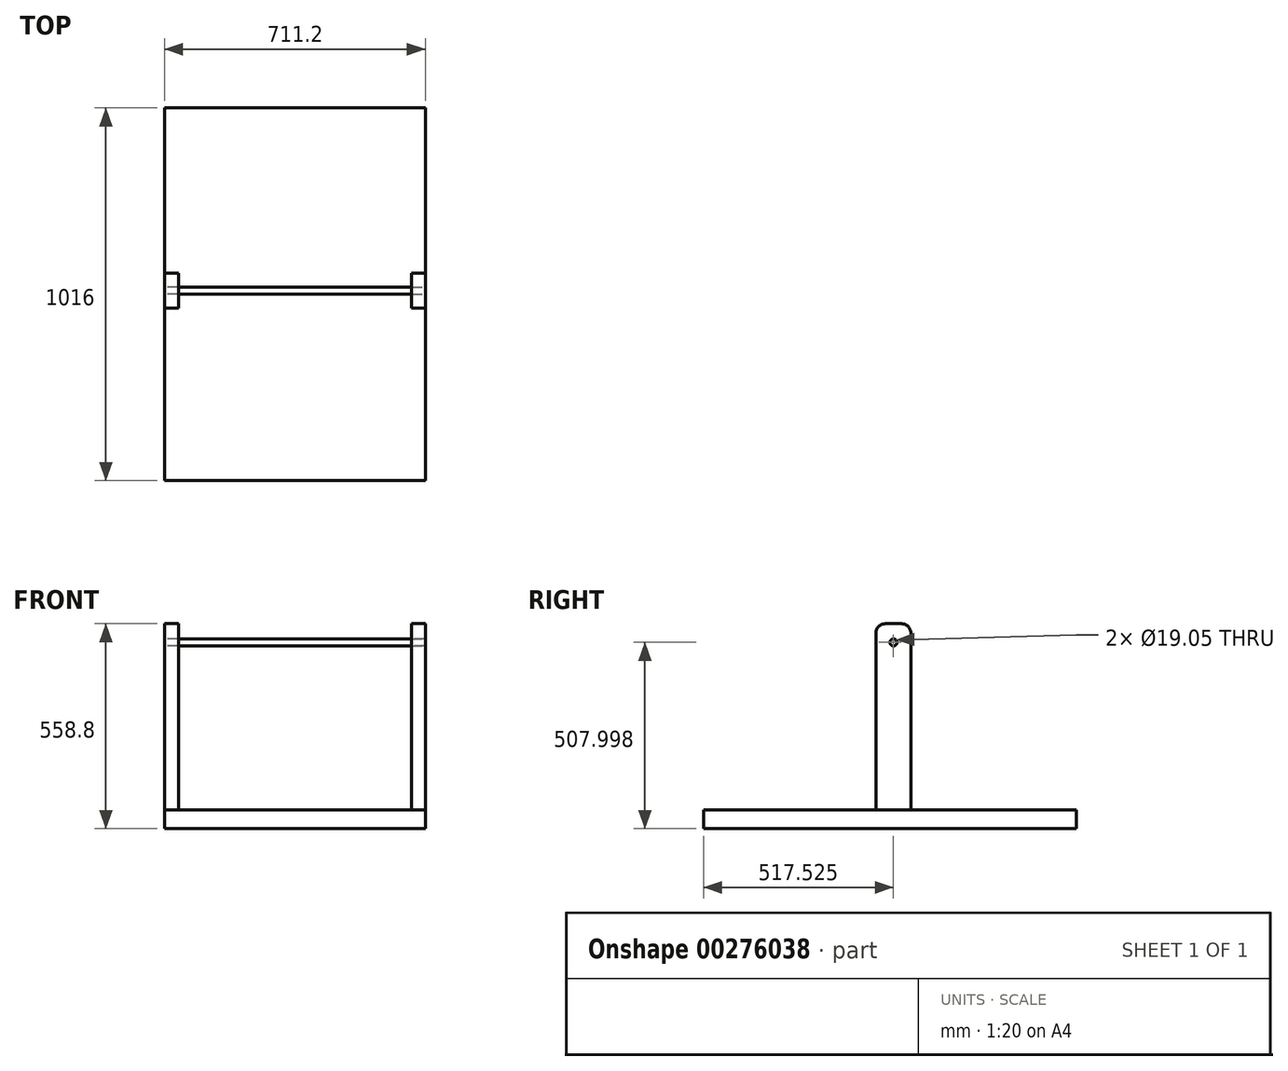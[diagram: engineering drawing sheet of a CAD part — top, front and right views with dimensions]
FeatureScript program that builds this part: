
annotation { "Feature Type Name" : "Feature", "Feature Type Description" : "" }
export const myFeature = defineFeature(function(context is Context, id is Id, definition is map)
    precondition{}
    {
        {
            var Q0;
            Q0=qCreatedBy(makeId("Front.planeOp"),FACE);
            var sketch = newSketch(context, id + "F0", { "sketchPlane" : qUnion([Q0])});
            skLineSegment(sketch, "E0", {"start": v(-62.9, 34.99) * mm, "end": v(-62.9, -15.81) * mm});
            skLineSegment(sketch, "E1", {"start": v(-62.9, -15.81) * mm, "end": v(648.3, -15.81) * mm});
            skLineSegment(sketch, "E2", {"start": v(648.3, -15.81) * mm, "end": v(648.3, 34.99) * mm});
            skLineSegment(sketch, "E3", {"start": v(648.3, 34.99) * mm, "end": v(-62.9, 34.99) * mm});
            skSolve(sketch);
        }
        {
            var Q0;
            Q0 = qSketchRegion(id + "F0", true);
            extrude(context, id + "F1", {"entities" : qUnion([Q0]), "depth" : 1016 * mm});
        }
        {
            var Q0;
            Q0=makeQuery(id+"F1.opExtrude","SWEPT_FACE",FACE,{"disambiguationData":[OSD([sQuery(id+"F0.wireOp",EDGE,"E0")])]});
            var sketch = newSketch(context, id + "F2", { "sketchPlane" : qUnion([Q0])});
            skLineSegment(sketch, "E4", {"start": v(450.85, 34.99) * mm, "end": v(450.85, 517.59) * mm});
            skLineSegment(sketch, "E5", {"start": v(546.1, 34.99) * mm, "end": v(546.1, 517.59) * mm});
            skLineSegment(sketch, "E6", {"start": v(546.1, 34.99) * mm, "end": v(450.85, 34.99) * mm});
            skLineSegment(sketch, "E7", {"start": v(476.25, 542.99) * mm, "end": v(520.7, 542.99) * mm});
            skLineSegment(sketch, "E8", {"start": v(498.48, 542.99) * mm, "end": v(498.48, 492.19) * mm});
            skCircle(sketch, "E9", {"center": v(498.48, 492.19) * mm, "radius": 9.53 * mm});
            skPoint(sketch, "E10.visualSharp", {"position": v(450.85, 542.99) * mm});
            skArc(sketch, "E10.filletArc", {"start": v(476.25, 542.99) * mm, "mid": v(458.29, 535.55) * mm, "end": v(450.85, 517.59) * mm});
            skPoint(sketch, "E11.visualSharp", {"position": v(546.1, 542.99) * mm});
            skArc(sketch, "E11.filletArc", {"start": v(546.1, 517.59) * mm, "mid": v(538.66, 535.55) * mm, "end": v(520.7, 542.99) * mm});
            skLineSegment(sketch, "E12", {"start": v(1016, 34.99) * mm, "end": v(0, 34.99) * mm});
            skSolve(sketch);
        }
        {
            var Q0;
            Q0 = qSketchRegion(id + "F2", true);
            extrude(context, id + "F3", {"entities" : qUnion([Q0]), "oppositeDirection" : true, "depth" : 38.1 * mm});
        }
        {
            var Q0;
            Q0=makeQuery(id+"F1.opExtrude","SWEPT_FACE",FACE,{"disambiguationData":[OSD([sQuery(id+"F0.wireOp",EDGE,"E2")])]});
            var sketch = newSketch(context, id + "F4", { "sketchPlane" : qUnion([Q0])});
            skLineSegment(sketch, "E13", {"start": v(-1016, 34.99) * mm, "end": v(-546.1, 34.99) * mm});
            skLineSegment(sketch, "E14", {"start": v(0, 34.99) * mm, "end": v(-450.85, 34.99) * mm});
            skLineSegment(sketch, "E15", {"start": v(-546.1, 34.99) * mm, "end": v(-546.1, 517.59) * mm});
            skLineSegment(sketch, "E16", {"start": v(-450.85, 34.99) * mm, "end": v(-450.85, 517.59) * mm});
            skLineSegment(sketch, "E17", {"start": v(-520.7, 542.99) * mm, "end": v(-476.25, 542.99) * mm});
            skPoint(sketch, "E18.visualSharp", {"position": v(-546.1, 542.99) * mm});
            skArc(sketch, "E18.filletArc", {"start": v(-520.7, 542.99) * mm, "mid": v(-538.66, 535.55) * mm, "end": v(-546.1, 517.59) * mm});
            skPoint(sketch, "E19.visualSharp", {"position": v(-450.85, 542.99) * mm});
            skArc(sketch, "E19.filletArc", {"start": v(-450.85, 517.59) * mm, "mid": v(-458.29, 535.55) * mm, "end": v(-476.25, 542.99) * mm});
            skLineSegment(sketch, "E20", {"start": v(-498.48, 542.99) * mm, "end": v(-498.48, 492.19) * mm});
            skCircle(sketch, "E21", {"center": v(-498.48, 492.19) * mm, "radius": 9.53 * mm});
            skSolve(sketch);
        }
        {
            var Q0;
            {var subQ1=sQuery(id+"F4.wireOp",EDGE,"E15");Q0=makeQuery(id+"F4.imprint","IMPRINT",FACE,{"disambiguationData":[TD([[makeQuery(id+"F4.imprint","IMPRINT",EDGE,{"derivedFrom":subQ1}),-1.0]])]});}
            extrude(context, id + "F5", {"entities" : qUnion([Q0]), "oppositeDirection" : true, "depth" : 38.1 * mm});
        }
        {
            var Q0;
            Q0=makeQuery(id+"F3.opExtrude","CAP_FACE",FACE,{"disambiguationData":[OSD([sQuery(id+"F2.wireOp",EDGE,"E4"),sQuery(id+"F2.wireOp",EDGE,"E5"),sQuery(id+"F2.wireOp",EDGE,"E7"),sQuery(id+"F2.wireOp",EDGE,"E9"),sQuery(id+"F2.wireOp",EDGE,"E10.filletArc"),sQuery(id+"F2.wireOp",EDGE,"E11.filletArc"),sQuery(id+"F2.wireOp",EDGE,"E12")])],"isStart":false});
            var sketch = newSketch(context, id + "F6", { "sketchPlane" : qUnion([Q0])});
            skCircle(sketch, "E22", {"center": v(-498.48, 492.19) * mm, "radius": 9.53 * mm});
            skSolve(sketch);
        }
        {
            var Q0;
            Q0 = qSketchRegion(id + "F6", true);
            extrude(context, id + "F7", {"entities" : qUnion([Q0]), "depth" : 711.2 * mm});
        }
        {
            var Q0;
            Q0=makeQuery(id+"F7.opExtrude","SWEPT_BODY",BODY,{"disambiguationData":[OSD([sQuery(id+"F6.wireOp",EDGE,"E22")])]});
            transform(context, id + "F8", {"entities" : qUnion([Q0]), "transformType" : TransformType.TRANSLATION_3D, "dx" : -38.1 * mm, "dy" : 0 * mm, "dz" : 0 * mm, "makeCopy" : false});
        }
    });
